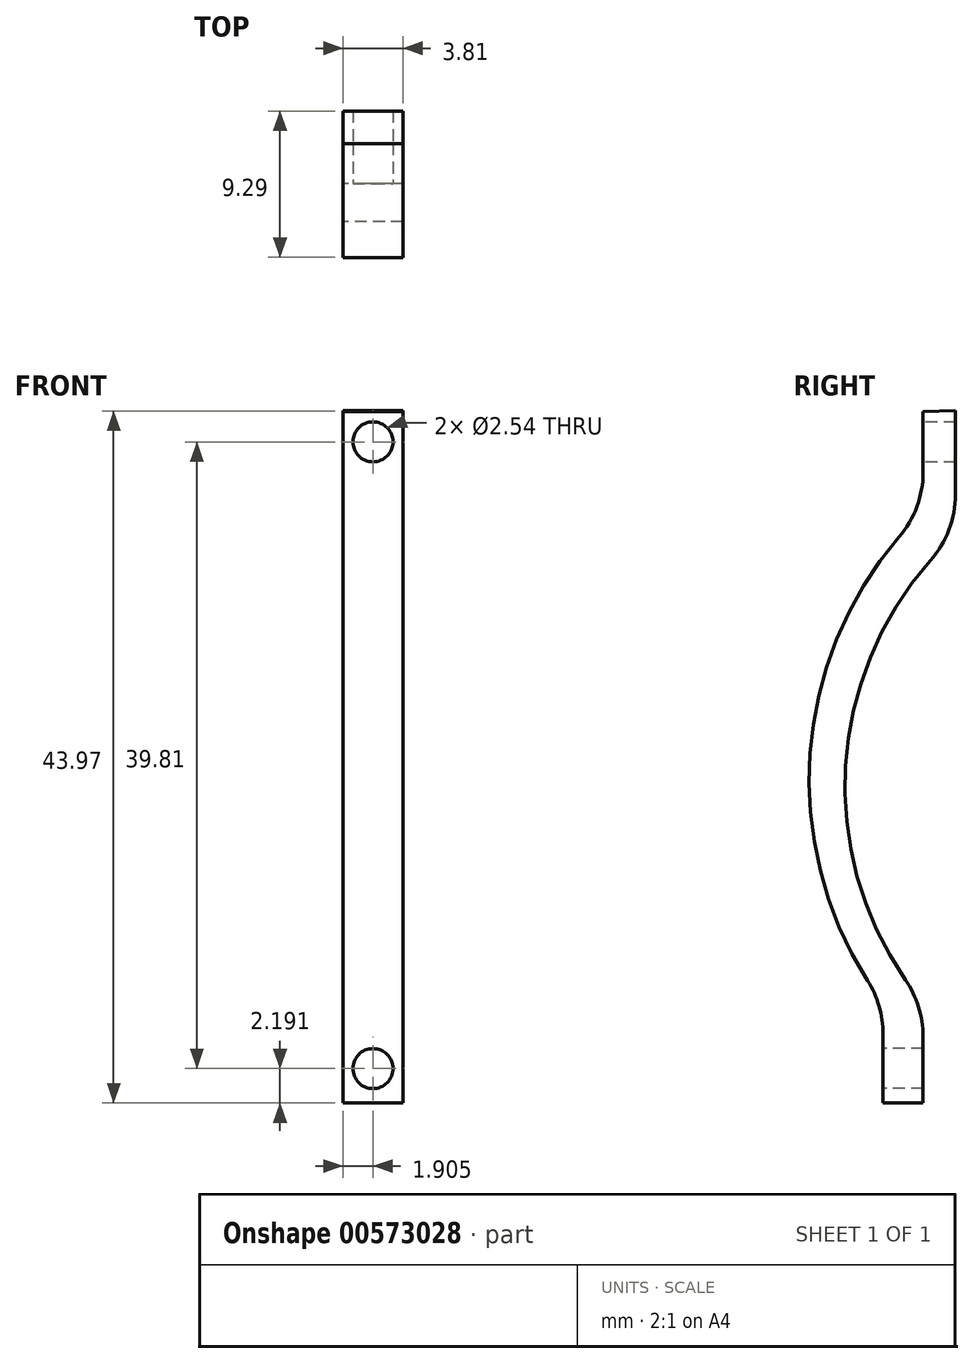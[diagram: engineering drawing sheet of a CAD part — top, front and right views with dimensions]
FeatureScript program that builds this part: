
annotation { "Feature Type Name" : "Feature", "Feature Type Description" : "" }
export const myFeature = defineFeature(function(context is Context, id is Id, definition is map)
    precondition{}
    {
        {
            var Q0;
            Q0=qCreatedBy(makeId("Right.planeOp"),FACE);
            var sketch = newSketch(context, id + "F0", { "sketchPlane" : qUnion([Q0])});
            skLineSegment(sketch, "E0", {"start": v(0, 0) * mm, "end": v(0, 4.38) * mm});
            skLineSegment(sketch, "E1", {"start": v(0, 0) * mm, "end": v(2.54, 0) * mm});
            skLineSegment(sketch, "E2", {"start": v(2.54, 0) * mm, "end": v(2.54, 4.23) * mm});
            skLineSegment(sketch, "E3", {"start": v(31.99, 0) * mm, "end": v(31.99, 6.38) * mm});
            skArc(sketch, "E4", {"start": v(1.01, 35.95) * mm, "mid": v(-4.64, 22.2) * mm, "end": v(-1, 7.79) * mm});
            skArc(sketch, "E5", {"start": v(3, 34.46) * mm, "mid": v(-2.38, 21.42) * mm, "end": v(1.41, 7.84) * mm});
            skLineSegment(sketch, "E6", {"start": v(2.54, 40.08) * mm, "end": v(2.54, 43.92) * mm});
            skLineSegment(sketch, "E7", {"start": v(4.6, 38.67) * mm, "end": v(4.6, 43.97) * mm});
            skLineSegment(sketch, "E8", {"start": v(2.54, 43.92) * mm, "end": v(4.6, 43.97) * mm});
            skPoint(sketch, "E9.visualSharp", {"position": v(2.54, 37.57) * mm});
            skArc(sketch, "E9.filletArc", {"start": v(1.01, 35.95) * mm, "mid": v(2.15, 37.88) * mm, "end": v(2.54, 40.08) * mm});
            skPoint(sketch, "E10.visualSharp", {"position": v(4.6, 36.08) * mm});
            skArc(sketch, "E10.filletArc", {"start": v(3, 34.46) * mm, "mid": v(4.19, 36.42) * mm, "end": v(4.6, 38.67) * mm});
            skPoint(sketch, "E11.visualSharp", {"position": v(2.54, 6.35) * mm});
            skArc(sketch, "E11.filletArc", {"start": v(2.54, 4.23) * mm, "mid": v(2.25, 6.12) * mm, "end": v(1.41, 7.84) * mm});
            skPoint(sketch, "E12.visualSharp", {"position": v(0, 6.35) * mm});
            skArc(sketch, "E12.filletArc", {"start": v(0, 4.38) * mm, "mid": v(-0.25, 6.16) * mm, "end": v(-1, 7.79) * mm});
            skSolve(sketch);
        }
        {
            var Q0;
            Q0=makeQuery(id+"F0.imprint","IMPRINT",FACE,{"disambiguationData":[TD([[makeQuery(id+"F0.imprint","IMPRINT",EDGE,{"derivedFrom":sQuery(id+"F0.wireOp",EDGE,"E0")}),-1.0]])]});
            extrude(context, id + "F1", {"entities" : qUnion([Q0]), "depth" : 3.8 * mm, "offsetDistance" : 25.4 * mm});
        }
        {
            var Q0;
            Q0=makeQuery(id+"F1.opExtrude","SWEPT_FACE",FACE,{"disambiguationData":[OSD([sQuery(id+"F0.wireOp",EDGE,"E6")])]});
            var sketch = newSketch(context, id + "F2", { "sketchPlane" : qUnion([Q0])});
            skCircle(sketch, "E13", {"center": v(1.9, 42) * mm, "radius": 1.27 * mm});
            skSolve(sketch);
        }
        {
            var Q0;
            Q0 = qSketchRegion(id + "F2", true);
            extrude(context, id + "F3", {"entities" : qUnion([Q0]), "operationType" : NewBodyOperationType.REMOVE, "oppositeDirection" : true, "depth" : 25.4 * mm, "offsetDistance" : 25.4 * mm});
        }
        {
            var Q0;
            Q0=makeQuery(id+"F1.opExtrude","SWEPT_FACE",FACE,{"disambiguationData":[OSD([sQuery(id+"F0.wireOp",EDGE,"E0")])]});
            var sketch = newSketch(context, id + "F4", { "sketchPlane" : qUnion([Q0])});
            skCircle(sketch, "E14", {"center": v(1.9, 2.2) * mm, "radius": 1.27 * mm});
            skSolve(sketch);
        }
        {
            var Q0;
            Q0 = qSketchRegion(id + "F4", true);
            extrude(context, id + "F5", {"entities" : qUnion([Q0]), "operationType" : NewBodyOperationType.REMOVE, "oppositeDirection" : true, "depth" : 9.5 * mm, "offsetDistance" : 25.4 * mm});
        }
    });
